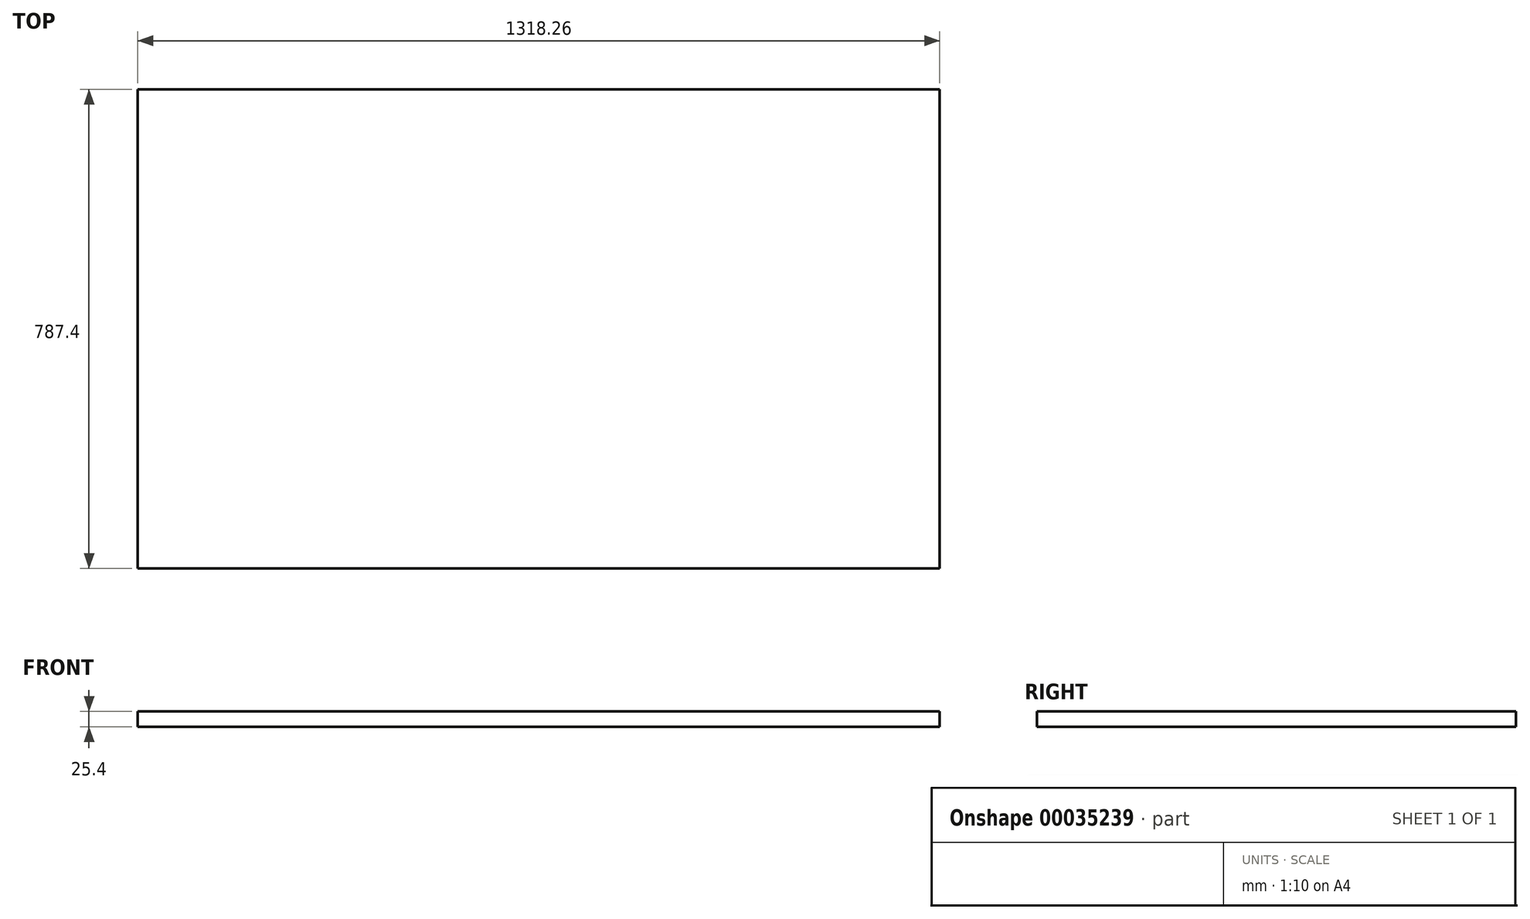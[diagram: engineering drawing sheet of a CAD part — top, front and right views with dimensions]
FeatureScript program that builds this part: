
annotation { "Feature Type Name" : "Feature", "Feature Type Description" : "" }
export const myFeature = defineFeature(function(context is Context, id is Id, definition is map)
    precondition{}
    {
        {
            var Q0;
            Q0=qCreatedBy(makeId("Top.planeOp"),FACE);
            var sketch = newSketch(context, id + "F0", { "sketchPlane" : qUnion([Q0])});
            skLineSegment(sketch, "E0.rect.bottom", {"start": v(681.04, -393.7) * mm, "end": v(-637.22, -393.7) * mm});
            skLineSegment(sketch, "E0.rect.top", {"start": v(681.04, 393.7) * mm, "end": v(-637.22, 393.7) * mm});
            skLineSegment(sketch, "E0.rect.left", {"start": v(681.04, -393.7) * mm, "end": v(681.04, 393.7) * mm});
            skLineSegment(sketch, "E0.rect.right", {"start": v(-637.22, -393.7) * mm, "end": v(-637.22, 393.7) * mm});
            skPoint(sketch, "E0.rect.middle", {"position": v(21.91, 0) * mm});
            skSolve(sketch);
        }
        {
            var Q0;
            Q0=makeQuery(id+"F0.imprint","IMPRINT",FACE,{"disambiguationData":[TD([[makeQuery(id+"F0.imprint","IMPRINT",EDGE,{"derivedFrom":sQuery(id+"F0.wireOp",EDGE,"E0.rect.bottom")}),-1.0]])]});
            extrude(context, id + "F1", {"entities" : qUnion([Q0]), "depth" : 25.4 * mm});
        }
    });
